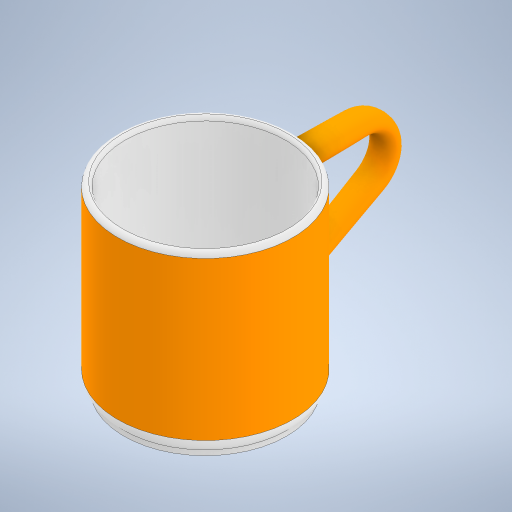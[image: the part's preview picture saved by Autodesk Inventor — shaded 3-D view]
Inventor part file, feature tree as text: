
AUTODESK INVENTOR PART (.ipt)
format: ipt  version: 2024.2 (Build 282272000, 272)  size: 357,888 bytes
history: native  units: mm
features: sketch x8, plane x2, other x1, revolve x1, shell x1, loft x1, fillet x1, extrude x1
ambient origin geometry x8: Origin, YZ Plane, XZ Plane, XY Plane, X Axis, Y Axis, Z Axis, Center Point
bodies: Solid1 (feature_tree)
feature tree (16):
  other  "CrossSection1"
  revolve  "Revolution1"  [1 undecoded]
  shell  "Shell1"  Thickness=32.5mm
  sketch  "Sketch2"  dims[d8=360.0deg d9=3.0mm]
  sketch  "Sketch3"  dims[d10=0.5mm d11=2.0mm d12=0.0mm d13=20.0mm d23=6.0mm]
  plane  "Work Plane1"
  sketch  "Sketch4"  dims[d24=4.0mm d25=5.0mm]
  plane  "Work Plane2"
  loft  "Loft1"
  fillet  "Fillet1"  Radius=6.0mm
  sketch  "Sketch6"  dims[d27=0.0mm d28=90.0deg]
  extrude  "Extrusion1"  Depth=5.0mm
  sketch  "3D Sketch1"
  sketch  "Sketch1"  dims[d4=35.0mm d5=65.0mm d7=32.5mm]
  sketch  "Sketch5"  dims[d26=3.0mm]
  sketch  "Sketch7"  dims[d29=0.0mm d30=90.0deg d31=0.0mm d32=90.0deg d33=2.0mm d34=62.0mm d35=65.0mm d36=2.0mm d37=0.0mm]
note: 1 required parameter value undecoded (feature->parameter linkage not recoverable at this tier; creation-order binding heuristic only, values carry confidence <= 0.55)
